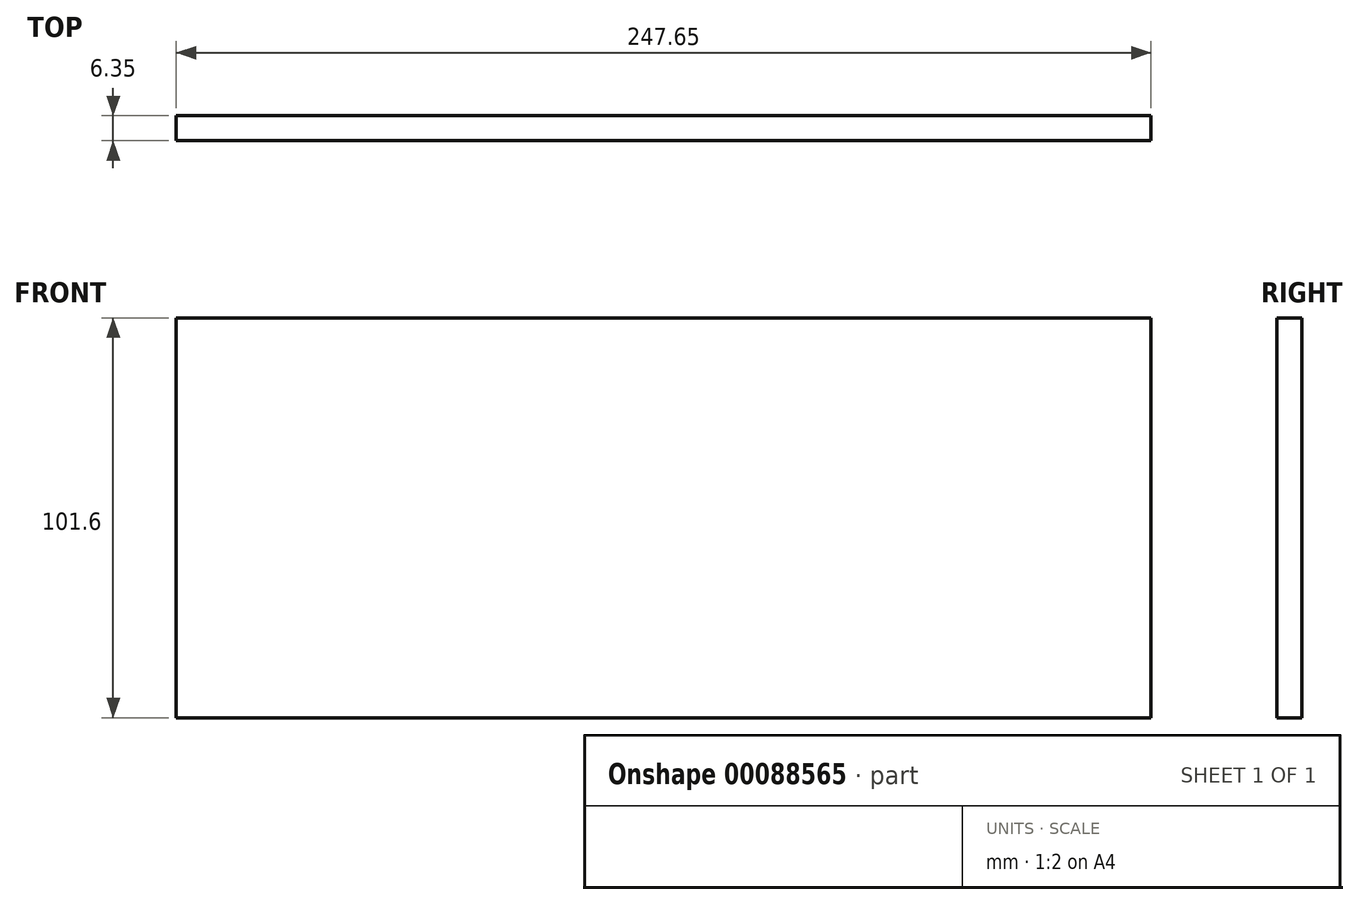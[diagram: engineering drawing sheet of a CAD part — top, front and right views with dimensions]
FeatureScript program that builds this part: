
annotation { "Feature Type Name" : "Feature", "Feature Type Description" : "" }
export const myFeature = defineFeature(function(context is Context, id is Id, definition is map)
    precondition{}
    {
        {
            var Q0;
            Q0=qCreatedBy(makeId("Front.planeOp"),FACE);
            var sketch = newSketch(context, id + "F0", { "sketchPlane" : qUnion([Q0])});
            skLineSegment(sketch, "E0.bottom", {"start": v(-51.91, 88.05) * mm, "end": v(195.74, 88.05) * mm});
            skLineSegment(sketch, "E0.top", {"start": v(-51.91, -13.55) * mm, "end": v(195.74, -13.55) * mm});
            skLineSegment(sketch, "E0.left", {"start": v(-51.91, 88.05) * mm, "end": v(-51.91, -13.55) * mm});
            skLineSegment(sketch, "E0.right", {"start": v(195.74, 88.05) * mm, "end": v(195.74, -13.55) * mm});
            skSolve(sketch);
        }
        {
            var Q0;
            Q0=makeQuery(id+"F0.imprint","IMPRINT",FACE,{"disambiguationData":[TD([[makeQuery(id+"F0.imprint","IMPRINT",EDGE,{"derivedFrom":sQuery(id+"F0.wireOp",EDGE,"E0.bottom")}),-1.0]])]});
            extrude(context, id + "F1", {"entities" : qUnion([Q0]), "depth" : 6.35 * mm});
        }
    });
